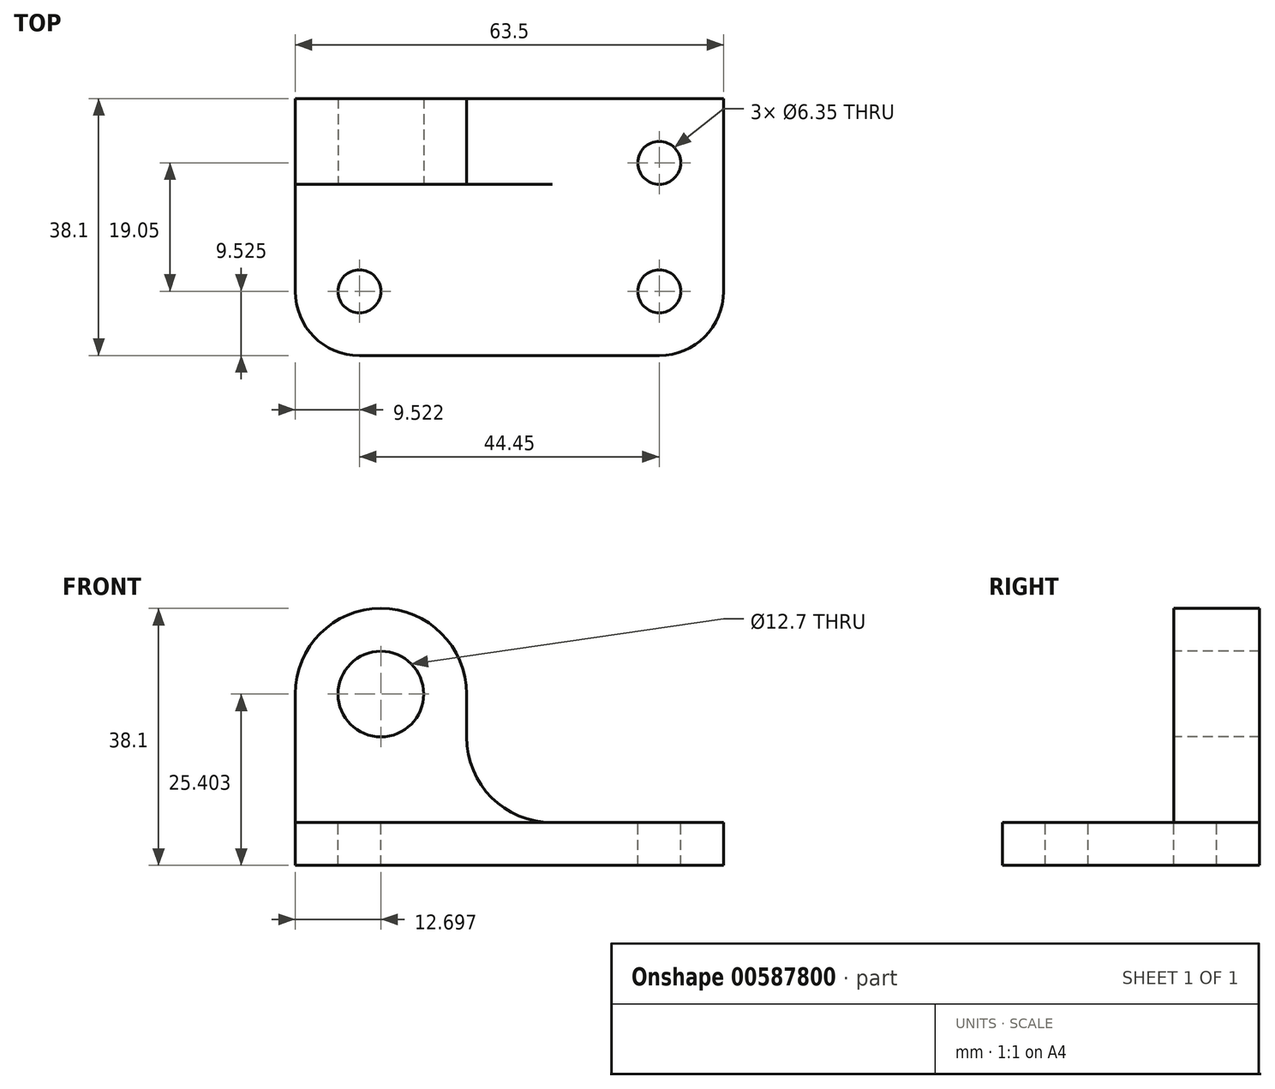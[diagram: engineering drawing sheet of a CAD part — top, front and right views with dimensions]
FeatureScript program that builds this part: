
annotation { "Feature Type Name" : "Feature", "Feature Type Description" : "" }
export const myFeature = defineFeature(function(context is Context, id is Id, definition is map)
    precondition{}
    {
        {
            var Q0;
            Q0=qCreatedBy(makeId("Front.planeOp"),FACE);
            var sketch = newSketch(context, id + "F0", { "sketchPlane" : qUnion([Q0])});
            skLineSegment(sketch, "E0", {"start": v(-73.62, 52.93) * mm, "end": v(-73.62, 14.83) * mm});
            skLineSegment(sketch, "E1", {"start": v(-73.62, 14.83) * mm, "end": v(-10.12, 14.83) * mm});
            skLineSegment(sketch, "E2", {"start": v(-10.12, 14.83) * mm, "end": v(-10.12, 21.18) * mm});
            skLineSegment(sketch, "E3", {"start": v(-10.12, 21.18) * mm, "end": v(-35.52, 21.18) * mm});
            skLineSegment(sketch, "E4", {"start": v(-35.52, 21.18) * mm, "end": v(-35.52, 52.93) * mm});
            skLineSegment(sketch, "E5", {"start": v(-35.52, 52.93) * mm, "end": v(-73.62, 52.93) * mm});
            skSolve(sketch);
        }
        {
            var Q0;
            Q0 = qSketchRegion(id + "F0", true);
            extrude(context, id + "F1", {"entities" : qUnion([Q0]), "depth" : 38.1 * mm, "offsetDistance" : 25.4 * mm});
        }
        {
            var Q0;
            Q0=makeQuery(id+"F1.opExtrude","CAP_FACE",FACE,{"disambiguationData":[OSD([sQuery(id+"F0.wireOp",EDGE,"E0"),sQuery(id+"F0.wireOp",EDGE,"E1"),sQuery(id+"F0.wireOp",EDGE,"E2"),sQuery(id+"F0.wireOp",EDGE,"E3"),sQuery(id+"F0.wireOp",EDGE,"E4"),sQuery(id+"F0.wireOp",EDGE,"E5")])],"isStart":false});
            var sketch = newSketch(context, id + "F2", { "sketchPlane" : qUnion([Q0])});
            skLineSegment(sketch, "E6", {"start": v(-73.62, 52.93) * mm, "end": v(-73.62, 21.18) * mm});
            skLineSegment(sketch, "E7", {"start": v(-73.62, 21.18) * mm, "end": v(-35.52, 21.18) * mm});
            skLineSegment(sketch, "E8", {"start": v(-35.52, 21.18) * mm, "end": v(-35.52, 52.93) * mm});
            skLineSegment(sketch, "E9", {"start": v(-35.52, 52.93) * mm, "end": v(-73.62, 52.93) * mm});
            skSolve(sketch);
        }
        {
            var Q0;
            Q0 = qSketchRegion(id + "F2", true);
            extrude(context, id + "F3", {"entities" : qUnion([Q0]), "operationType" : NewBodyOperationType.REMOVE, "oppositeDirection" : true, "depth" : 25.4 * mm, "offsetDistance" : 25.4 * mm});
        }
        {
            var Q0;
            Q0=makeQuery(id+"F3.boolean.opBoolean","MERGE",FACE,{"derivedFrom":[makeQuery(id+"F1.opExtrude","SWEPT_FACE",FACE,{"disambiguationData":[OSD([sQuery(id+"F0.wireOp",EDGE,"E3")])]}),makeQuery(id+"F3.opExtrude","SWEPT_FACE",FACE,{"disambiguationData":[OSD([sQuery(id+"F2.wireOp",EDGE,"E7")])]})]});
            var sketch = newSketch(context, id + "F4", { "sketchPlane" : qUnion([Q0])});
            skCircle(sketch, "E10", {"center": v(-19.65, -28.58) * mm, "radius": 3.18 * mm});
            skArc(sketch, "E11", {"start": v(-19.65, -38.1) * mm, "mid": v(-12.91, -35.31) * mm, "end": v(-10.12, -28.58) * mm});
            skCircle(sketch, "E12", {"center": v(-64.1, -28.58) * mm, "radius": 3.18 * mm});
            skArc(sketch, "E13", {"start": v(-73.62, -28.58) * mm, "mid": v(-70.83, -35.31) * mm, "end": v(-64.1, -38.1) * mm});
            skSolve(sketch);
        }
        {
            var Q0;
            Q0 = qSketchRegion(id + "F4", true);
            var Q1;
            {var subQ0=sQuery(id+"F4.wireOp",EDGE,"E13");Q1=makeQuery(id+"F4.imprint","IMPRINT",FACE,{"disambiguationData":[TD([[makeQuery(id+"F4.imprint","IMPRINT",EDGE,{"derivedFrom":subQ0}),-1.0]])]});}
            var Q2;
            {var subQ0=sQuery(id+"F4.wireOp",EDGE,"E11");Q2=makeQuery(id+"F4.imprint","IMPRINT",FACE,{"disambiguationData":[TD([[makeQuery(id+"F4.imprint","IMPRINT",EDGE,{"derivedFrom":subQ0}),-1.0]])]});}
            extrude(context, id + "F5", {"entities" : qUnion([Q0, Q1, Q2]), "operationType" : NewBodyOperationType.REMOVE, "oppositeDirection" : true, "depth" : 25.4 * mm, "offsetDistance" : 25.4 * mm});
        }
        {
            var Q0;
            Q0=makeQuery(id+"F3.boolean.opBoolean","MERGE",FACE,{"derivedFrom":[makeQuery(id+"F1.opExtrude","SWEPT_FACE",FACE,{"disambiguationData":[OSD([sQuery(id+"F0.wireOp",EDGE,"E3")])]}),makeQuery(id+"F3.opExtrude","SWEPT_FACE",FACE,{"disambiguationData":[OSD([sQuery(id+"F2.wireOp",EDGE,"E7")])]})]});
            var sketch = newSketch(context, id + "F6", { "sketchPlane" : qUnion([Q0])});
            skCircle(sketch, "E14", {"center": v(-19.65, -9.52) * mm, "radius": 3.17 * mm});
            skSolve(sketch);
        }
        {
            var Q0;
            Q0 = qSketchRegion(id + "F6", true);
            extrude(context, id + "F7", {"entities" : qUnion([Q0]), "operationType" : NewBodyOperationType.REMOVE, "oppositeDirection" : true, "depth" : 25.4 * mm, "offsetDistance" : 25.4 * mm});
        }
        {
            var Q0;
            Q0=makeQuery(id+"F3.boolean.opBoolean","COPY",FACE,{"derivedFrom":makeQuery(id+"F3.opExtrude","CAP_FACE",FACE,{"disambiguationData":[OSD([sQuery(id+"F2.wireOp",EDGE,"E6"),sQuery(id+"F2.wireOp",EDGE,"E7"),sQuery(id+"F2.wireOp",EDGE,"E8"),sQuery(id+"F2.wireOp",EDGE,"E9")])],"isStart":false})});
            var sketch = newSketch(context, id + "F8", { "sketchPlane" : qUnion([Q0])});
            skCircle(sketch, "E15", {"center": v(-60.92, 40.23) * mm, "radius": 6.35 * mm});
            skSolve(sketch);
        }
        {
            var Q0;
            Q0 = qSketchRegion(id + "F8", true);
            extrude(context, id + "F9", {"entities" : qUnion([Q0]), "operationType" : NewBodyOperationType.REMOVE, "oppositeDirection" : true, "depth" : 25.4 * mm, "offsetDistance" : 25.4 * mm});
        }
        {
            var Q0;
            Q0=makeQuery(id+"F3.boolean.opBoolean","COPY",FACE,{"derivedFrom":makeQuery(id+"F3.opExtrude","CAP_FACE",FACE,{"disambiguationData":[OSD([sQuery(id+"F2.wireOp",EDGE,"E6"),sQuery(id+"F2.wireOp",EDGE,"E7"),sQuery(id+"F2.wireOp",EDGE,"E8"),sQuery(id+"F2.wireOp",EDGE,"E9")])],"isStart":false})});
            var sketch = newSketch(context, id + "F10", { "sketchPlane" : qUnion([Q0])});
            skArc(sketch, "E16", {"start": v(-48.22, 40.23) * mm, "mid": v(-60.92, 52.93) * mm, "end": v(-73.62, 40.23) * mm});
            skArc(sketch, "E17", {"start": v(-48.22, 33.88) * mm, "mid": v(-44.5, 24.9) * mm, "end": v(-35.52, 21.18) * mm});
            skLineSegment(sketch, "E18", {"start": v(-48.22, 40.23) * mm, "end": v(-48.22, 33.88) * mm});
            skSolve(sketch);
        }
        {
            var Q0;
            Q0 = qSketchRegion(id + "F10", true);
            var Q1;
            Q1=makeQuery(id+"F10.imprint","IMPRINT",FACE,{"disambiguationData":[TD([[makeQuery(id+"F10.imprint","IMPRINT",EDGE,{"derivedFrom":sQuery(id+"F10.wireOp",EDGE,"E17")}),1.0]])]});
            var Q2;
            {var subQ0=sQuery(id+"F10.wireOp",EDGE,"E16");var subQ1=makeQuery(id+"F3.boolean.opBoolean","COPY",EDGE,{"derivedFrom":makeQuery(id+"F3.opExtrude","CAP_EDGE",EDGE,{"disambiguationData":[OSD([sQuery(id+"F2.wireOp",EDGE,"E6")])],"isStart":false})});var subQ2=makeQuery(id+"F10.imprint","INTERSECT",VERTEX,{"derivedFrom":[subQ1,subQ0]});Q2=makeQuery(id+"F10.imprint","IMPRINT",FACE,{"disambiguationData":[TD([[makeQuery(id+"F10.imprint","IMPRINT",EDGE,{"disambiguationData":[TD([[subQ2,1.0]])],"derivedFrom":subQ0}),-1.0]])]});}
            extrude(context, id + "F11", {"entities" : qUnion([Q0, Q1, Q2]), "operationType" : NewBodyOperationType.REMOVE, "oppositeDirection" : true, "depth" : 25.4 * mm, "offsetDistance" : 25.4 * mm});
        }
    });
